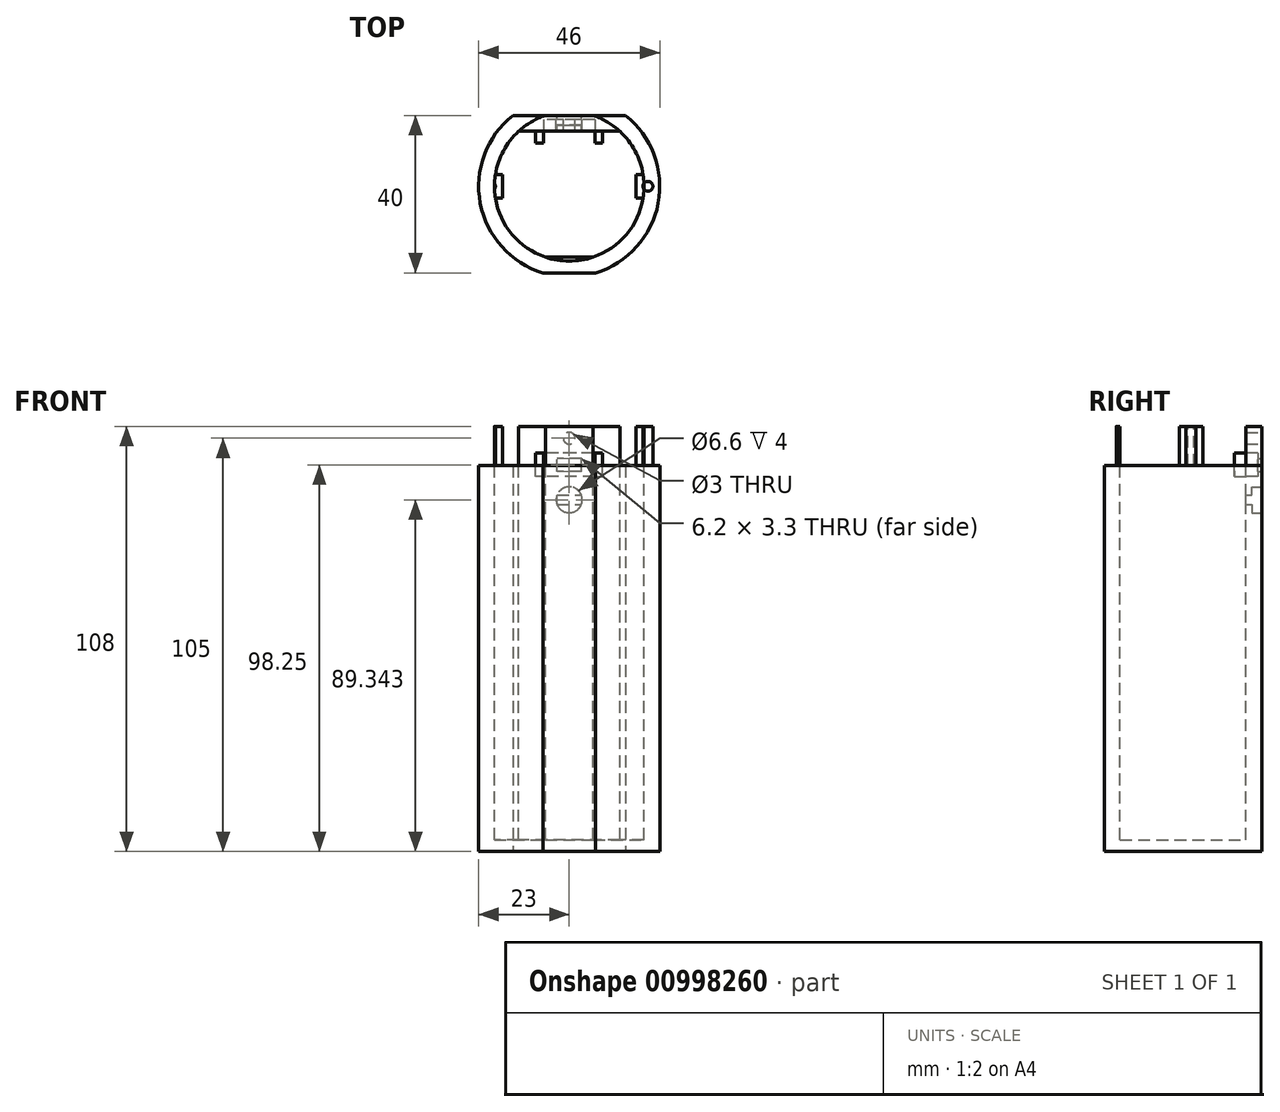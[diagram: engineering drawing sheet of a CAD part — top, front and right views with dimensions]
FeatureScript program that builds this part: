
annotation { "Feature Type Name" : "Feature", "Feature Type Description" : "" }
export const myFeature = defineFeature(function(context is Context, id is Id, definition is map)
    precondition{}
    {
        {
            var Q0;
            Q0=qCreatedBy(makeId("Top.planeOp"),FACE);
            var sketch = newSketch(context, id + "F0", { "sketchPlane" : qUnion([Q0])});
            skCircle(sketch, "E0", {"center": v(0, 0) * mm, "radius": 23 * mm});
            skLineSegment(sketch, "E1", {"start": v(-14.32, 18) * mm, "end": v(14.32, 18) * mm});
            skLineSegment(sketch, "E2", {"start": v(-6.7, -22) * mm, "end": v(6.7, -22) * mm});
            skSolve(sketch);
        }
        {
            var Q0;
            {var subQ0=sQuery(id+"F0.wireOp",EDGE,"E1");Q0=makeQuery(id+"F0.imprint","IMPRINT",FACE,{"disambiguationData":[TD([[makeQuery(id+"F0.imprint","IMPRINT",EDGE,{"derivedFrom":subQ0}),-1.0]])]});}
            extrude(context, id + "F1", {"entities" : qUnion([Q0]), "depth" : 108 * mm, "offsetDistance" : 25 * mm});
        }
        {
            var Q0;
            Q0=makeQuery(id+"F1.opExtrude","CAP_FACE",FACE,{"disambiguationData":[OSD([sQuery(id+"F0.wireOp",EDGE,"E0")])],"isStart":false});
            var sketch = newSketch(context, id + "F2", { "sketchPlane" : qUnion([Q0])});
            skArc(sketch, "E3.0", {"start": v(6.08, -18) * mm, "mid": v(18.59, -3.93) * mm, "end": v(12.85, 14) * mm});
            skLineSegment(sketch, "E3.1", {"start": v(-6.08, -18) * mm, "end": v(6.08, -18) * mm});
            skArc(sketch, "E3.2", {"start": v(-12.85, 14) * mm, "mid": v(-18.59, -3.93) * mm, "end": v(-6.08, -18) * mm});
            skLineSegment(sketch, "E3.3", {"start": v(12.85, 14) * mm, "end": v(-12.85, 14) * mm});
            skSolve(sketch);
        }
        {
            var Q0;
            Q0=makeQuery(id+"F2.imprint","IMPRINT",FACE,{"disambiguationData":[TD([[makeQuery(id+"F2.imprint","IMPRINT",EDGE,{"derivedFrom":sQuery(id+"F2.wireOp",EDGE,"e93e941d-6f13-4c6e-89ef-089453cd70ef.0")}),1.0]])]});
            var Q1;
            Q1=makeQuery(id+"F2.imprint","IMPRINT",FACE,{"disambiguationData":[TD([[makeQuery(id+"F2.imprint","IMPRINT",EDGE,{"derivedFrom":sQuery(id+"F2.wireOp",EDGE,"E3.0")}),1.0]])]});
            extrude(context, id + "F3", {"entities" : qUnion([Q0, Q1]), "operationType" : NewBodyOperationType.REMOVE, "oppositeDirection" : true, "depth" : 105 * mm, "offsetDistance" : 25 * mm});
        }
        {
            var Q0;
            Q0=makeQuery(id+"F1.opExtrude","SWEPT_FACE",FACE,{"disambiguationData":[OSD([sQuery(id+"F0.wireOp",EDGE,"E1")])]});
            var sketch = newSketch(context, id + "F4", { "sketchPlane" : qUnion([Q0])});
            skPoint(sketch, "E4.middle", {"position": v(0, 98.25) * mm});
            skLineSegment(sketch, "E5.bottom", {"start": v(-3.1, 96.6) * mm, "end": v(3.1, 96.6) * mm});
            skLineSegment(sketch, "E5.top", {"start": v(-3.1, 99.9) * mm, "end": v(3.1, 99.9) * mm});
            skLineSegment(sketch, "E5.left", {"start": v(-3.1, 96.6) * mm, "end": v(-3.1, 99.9) * mm});
            skLineSegment(sketch, "E5.right", {"start": v(3.1, 96.6) * mm, "end": v(3.1, 99.9) * mm});
            skCircle(sketch, "E6", {"center": v(0, 89.34) * mm, "radius": 3.3 * mm});
            skCircle(sketch, "E7", {"center": v(0, 105) * mm, "radius": 1.5 * mm});
            skSolve(sketch);
        }
        {
            var Q0;
            Q0=makeQuery(id+"F4.imprint","IMPRINT",FACE,{"disambiguationData":[TD([[makeQuery(id+"F4.imprint","IMPRINT",EDGE,{"derivedFrom":sQuery(id+"F4.wireOp",EDGE,"E5.bottom")}),1.0]])]});
            extrude(context, id + "F5", {"entities" : qUnion([Q0]), "operationType" : NewBodyOperationType.REMOVE, "oppositeDirection" : true, "depth" : 4 * mm, "offsetDistance" : 25 * mm});
        }
        {
            var Q0;
            Q0=makeQuery(id+"F4.imprint","IMPRINT",FACE,{"disambiguationData":[TD([[makeQuery(id+"F4.imprint","IMPRINT",EDGE,{"derivedFrom":sQuery(id+"F4.wireOp",EDGE,"E6")}),1.0]])]});
            extrude(context, id + "F6", {"entities" : qUnion([Q0]), "operationType" : NewBodyOperationType.REMOVE, "oppositeDirection" : true, "depth" : 2.5 * mm, "offsetDistance" : 25 * mm});
        }
        {
            var Q0;
            Q0=makeQuery(id+"F6.boolean.opBoolean","COPY",FACE,{"derivedFrom":makeQuery(id+"F6.opExtrude","CAP_FACE",FACE,{"disambiguationData":[OSD([sQuery(id+"F4.wireOp",EDGE,"E6")])],"isStart":false})});
            var sketch = newSketch(context, id + "F7", { "sketchPlane" : qUnion([Q0])});
            skLineSegment(sketch, "E8.bottom", {"start": v(3.07, 90.55) * mm, "end": v(-3.07, 90.55) * mm});
            skLineSegment(sketch, "E8.top", {"start": v(3.07, 88.14) * mm, "end": v(-3.07, 88.14) * mm});
            skPoint(sketch, "E8.middle", {"position": v(0, 89.34) * mm});
            skSolve(sketch);
        }
        {
            var Q0;
            {var subQ0=sQuery(id+"F7.wireOp",EDGE,"E8.bottom");Q0=makeQuery(id+"F7.imprint","IMPRINT",FACE,{"disambiguationData":[TD([[makeQuery(id+"F7.imprint","IMPRINT",EDGE,{"derivedFrom":subQ0}),1.0]])]});}
            extrude(context, id + "F8", {"entities" : qUnion([Q0]), "operationType" : NewBodyOperationType.REMOVE, "oppositeDirection" : true, "depth" : 1.5 * mm, "offsetDistance" : 25 * mm});
        }
        {
            var Q0;
            Q0=makeQuery(id+"F4.imprint","IMPRINT",FACE,{"disambiguationData":[TD([[makeQuery(id+"F4.imprint","IMPRINT",EDGE,{"derivedFrom":sQuery(id+"F4.wireOp",EDGE,"E7")}),1.0]])]});
            extrude(context, id + "F9", {"entities" : qUnion([Q0]), "operationType" : NewBodyOperationType.REMOVE, "oppositeDirection" : true, "depth" : 4 * mm, "offsetDistance" : 25 * mm});
        }
        {
            var Q0;
            Q0=makeQuery(id+"F3.boolean.opBoolean","COPY",FACE,{"derivedFrom":makeQuery(id+"F3.opExtrude","SWEPT_FACE",FACE,{"disambiguationData":[OSD([sQuery(id+"F2.wireOp",EDGE,"E3.3")])]})});
            var sketch = newSketch(context, id + "F10", { "sketchPlane" : qUnion([Q0])});
            skLineSegment(sketch, "E9.bottom", {"start": v(6.5, 101.25) * mm, "end": v(-6.5, 101.25) * mm});
            skLineSegment(sketch, "E9.top", {"start": v(6.5, 95.25) * mm, "end": v(-6.5, 95.25) * mm});
            skLineSegment(sketch, "E9.left", {"start": v(6.5, 101.25) * mm, "end": v(6.5, 95.25) * mm});
            skLineSegment(sketch, "E9.right", {"start": v(-6.5, 101.25) * mm, "end": v(-6.5, 95.25) * mm});
            skPoint(sketch, "E9.middle", {"position": v(0, 98.25) * mm});
            skPoint(sketch, "E9.middle.positionSnap0", {"position": v(-3.1, 98.25) * mm});
            skPoint(sketch, "E9.centerSnap0", {"position": v(-3.1, 98.25) * mm});
            skLineSegment(sketch, "E10.bottom", {"start": v(-6.5, 95.25) * mm, "end": v(-8.5, 95.25) * mm});
            skLineSegment(sketch, "E10.top", {"start": v(-6.5, 101.25) * mm, "end": v(-8.5, 101.25) * mm});
            skLineSegment(sketch, "E10.left", {"start": v(-6.5, 95.25) * mm, "end": v(-6.5, 101.25) * mm});
            skLineSegment(sketch, "E10.right", {"start": v(-8.5, 95.25) * mm, "end": v(-8.5, 101.25) * mm});
            skLineSegment(sketch, "E11.bottom", {"start": v(6.5, 95.25) * mm, "end": v(8.5, 95.25) * mm});
            skLineSegment(sketch, "E11.top", {"start": v(6.5, 101.25) * mm, "end": v(8.5, 101.25) * mm});
            skLineSegment(sketch, "E11.left", {"start": v(6.5, 95.25) * mm, "end": v(6.5, 101.25) * mm});
            skLineSegment(sketch, "E11.right", {"start": v(8.5, 95.25) * mm, "end": v(8.5, 101.25) * mm});
            skSolve(sketch);
        }
        {
            var Q0;
            Q0=makeQuery(id+"F10.imprint","IMPRINT",FACE,{"disambiguationData":[TD([[makeQuery(id+"F10.imprint","IMPRINT",EDGE,{"derivedFrom":sQuery(id+"F10.wireOp",EDGE,"E9.bottom")}),1.0]])]});
            extrude(context, id + "F11", {"entities" : qUnion([Q0]), "operationType" : NewBodyOperationType.REMOVE, "oppositeDirection" : true, "depth" : 3 * mm, "offsetDistance" : 25 * mm});
        }
        {
            var Q0;
            Q0=makeQuery(id+"F10.imprint","IMPRINT",FACE,{"disambiguationData":[TD([[makeQuery(id+"F10.imprint","IMPRINT",EDGE,{"derivedFrom":sQuery(id+"F10.wireOp",EDGE,"E10.bottom")}),-1.0]])]});
            var Q1;
            Q1=makeQuery(id+"F10.imprint","IMPRINT",FACE,{"disambiguationData":[TD([[makeQuery(id+"F10.imprint","IMPRINT",EDGE,{"derivedFrom":sQuery(id+"F10.wireOp",EDGE,"E11.bottom")}),1.0]])]});
            extrude(context, id + "F12", {"entities" : qUnion([Q0, Q1]), "operationType" : NewBodyOperationType.ADD, "depth" : 3 * mm, "offsetDistance" : 25 * mm});
        }
        {
            var Q0;
            Q0=makeQuery(id+"F1.opExtrude","CAP_FACE",FACE,{"disambiguationData":[OSD([sQuery(id+"F0.wireOp",EDGE,"E0"),sQuery(id+"F0.wireOp",EDGE,"E1"),sQuery(id+"F0.wireOp",EDGE,"E2")])],"isStart":false});
            var sketch = newSketch(context, id + "F13", { "sketchPlane" : qUnion([Q0])});
            skCircle(sketch, "E12", {"center": v(0, 0) * mm, "radius": 19 * mm});
            skCircle(sketch, "E13", {"center": v(-20, 0) * mm, "radius": 1.25 * mm});
            skLineSegment(sketch, "E14.bottom", {"start": v(-17, -3) * mm, "end": v(-18.76, -3) * mm});
            skLineSegment(sketch, "E14.top", {"start": v(-17, 3) * mm, "end": v(-18.76, 3) * mm});
            skLineSegment(sketch, "E14.left", {"start": v(-17, -3) * mm, "end": v(-17, 3) * mm});
            skLineSegment(sketch, "E15.MirrorCS", {"start": v(17, 3) * mm, "end": v(18.76, 3) * mm});
            skLineSegment(sketch, "E16.MirrorCS", {"start": v(17, -3) * mm, "end": v(17, 3) * mm});
            skPoint(sketch, "E17.MirrorP", {"position": v(20, 0) * mm});
            skCircle(sketch, "E18.MirrorC", {"center": v(20, 0) * mm, "radius": 1.25 * mm});
            skLineSegment(sketch, "E19.MirrorCS", {"start": v(17, -3) * mm, "end": v(18.76, -3) * mm});
            skSolve(sketch);
        }
        {
            var Q0;
            {var subQ0=sQuery(id+"F13.wireOp",EDGE,"E13");var subQ1=sQuery(id+"F13.wireOp",EDGE,"E12");var subQ2=makeQuery(id+"F13.imprint","INTERSECT",VERTEX,{"disambiguationData":[OD(0.0)],"derivedFrom":[subQ1,subQ0]});Q0=makeQuery(id+"F13.imprint","IMPRINT",FACE,{"disambiguationData":[TD([[makeQuery(id+"F13.imprint","IMPRINT",EDGE,{"disambiguationData":[TD([[subQ2,-1.0]])],"derivedFrom":subQ1}),-1.0]])]});}
            var Q1;
            {var subQ0=sQuery(id+"F13.wireOp",EDGE,"E18.MirrorC");var subQ1=sQuery(id+"F13.wireOp",EDGE,"E12");var subQ2=makeQuery(id+"F13.imprint","INTERSECT",VERTEX,{"disambiguationData":[OD(0.0)],"derivedFrom":[subQ1,subQ0]});Q1=makeQuery(id+"F13.imprint","IMPRINT",FACE,{"disambiguationData":[TD([[makeQuery(id+"F13.imprint","IMPRINT",EDGE,{"disambiguationData":[TD([[subQ2,-1.0]])],"derivedFrom":subQ1}),-1.0]])]});}
            extrude(context, id + "F14", {"entities" : qUnion([Q0, Q1]), "operationType" : NewBodyOperationType.REMOVE, "oppositeDirection" : true, "depth" : 10 * mm, "offsetDistance" : 25 * mm});
        }
        {
            var Q0;
            {var subQ0=sQuery(id+"F13.wireOp",EDGE,"E15.MirrorCS");Q0=makeQuery(id+"F13.imprint","IMPRINT",FACE,{"disambiguationData":[TD([[makeQuery(id+"F13.imprint","IMPRINT",EDGE,{"derivedFrom":subQ0}),-1.0]])]});}
            var Q1;
            {var subQ0=sQuery(id+"F13.wireOp",EDGE,"E14.bottom");Q1=makeQuery(id+"F13.imprint","IMPRINT",FACE,{"disambiguationData":[TD([[makeQuery(id+"F13.imprint","IMPRINT",EDGE,{"derivedFrom":subQ0}),-1.0]])]});}
            extrude(context, id + "F15", {"entities" : qUnion([Q0, Q1]), "operationType" : NewBodyOperationType.ADD, "oppositeDirection" : true, "depth" : 10 * mm, "offsetDistance" : 25 * mm});
        }
    });
